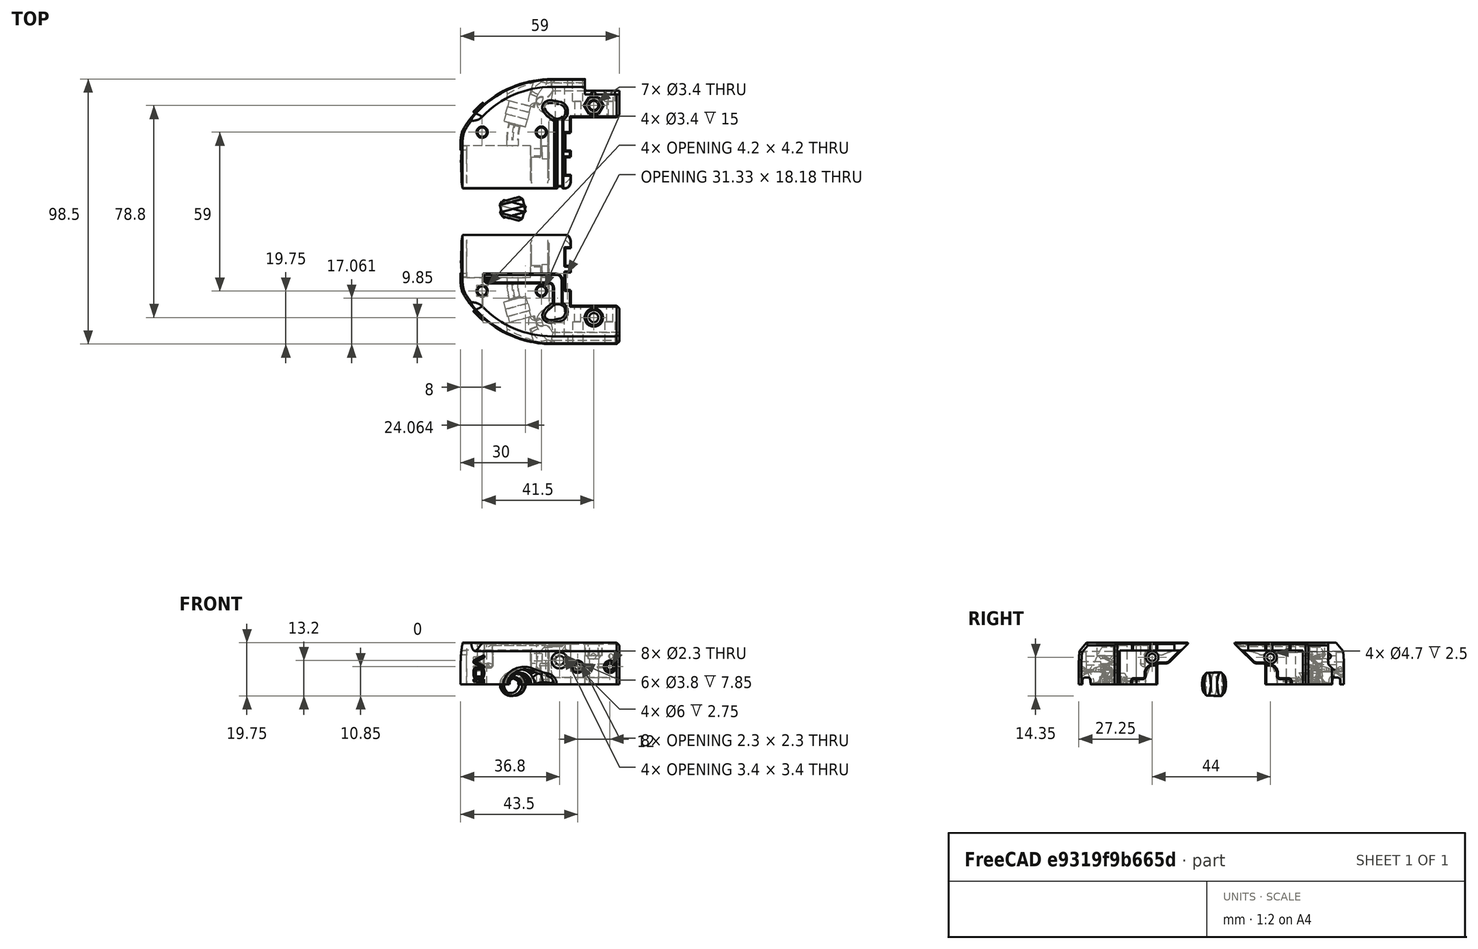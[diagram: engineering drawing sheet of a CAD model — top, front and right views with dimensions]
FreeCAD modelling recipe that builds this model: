
FCSTD DOCUMENT  (FreeCAD 0.18R16146 (Git))
Label: mosquito-toolhead-mod
License: All rights reserved
LicenseURL: http://en.wikipedia.org/wiki/All_rights_reserved
objects: Part::Cut×16, Part::Feature×12, Part::Cylinder×10, Part::Box×9, Part::MultiFuse×3, Part::Chamfer×2
note: 52 computed .brp shape members not serialized (recipe doc carries the construction recipe); baked Part::Feature solids carry a one-line shape summary decoded from their .brp

FEATURE [Part::Feature] Part__Feature154  label="Toolhead_Mosquito002"
  Placement = pos=(16.5,-1,0) rot=(0.707107,0,0.707107;3.14159rad)
  shape: bbox 59.02 x 41.29 x 24.92 mm, 349 faces (baked)
FEATURE [Part::Feature] Part__Feature155  label="Toolhead_Mosquito003"
  Placement = pos=(16.5,-1,0) rot=(0,1,0;1.5708rad)
  shape: bbox 59.02 x 41.29 x 24.92 mm, 379 faces (baked)
FEATURE [Part::Box] Box  label="Cube"
  AttacherType = Attacher::AttachEngine3D
  Height = 10
  Length = 12
  Placement = pos=(-4,-43,-10) rot=(0,0,1;0rad)
  Width = 10
FEATURE [Part::Cylinder] Cylinder  label="outer"
  Angle = 360
  AttacherType = Attacher::AttachEngine3D
  Height = 2.3
  Placement = pos=(0,0,0) rot=(0.983106,0.129428,0.129428;1.58783rad)
  Radius = 4.25
FEATURE [Part::Cylinder] Cylinder002  label="bore-vut"
  Angle = 360
  AttacherType = Attacher::AttachEngine3D
  Height = 2.6
  Placement = pos=(-0.67293,2.51141,-1e-15) rot=(0.983106,0.129428,0.129428;1.58783rad)
  Radius = 4.35
FEATURE [Part::Cylinder] Cylinder003  label="inner"
  Angle = 360
  AttacherType = Attacher::AttachEngine3D
  Height = 2.3
  Placement = pos=(0,0,0) rot=(0.983106,0.129428,0.129428;1.58783rad)
  Radius = 4.1
FEATURE [Part::Box] Box001  label="Cube001"
  AttacherType = Attacher::AttachEngine3D
  Height = 10
  Length = 12
  Placement = pos=(-4,-43,-10) rot=(0,0,1;0rad)
  Width = 10
FEATURE [Part::Box] Box002  label="Cube002"
  AttacherType = Attacher::AttachEngine3D
  Height = 10
  Length = 12
  Placement = pos=(-4,-43,-10) rot=(0,0,1;0rad)
  Width = 10
FEATURE [Part::Cylinder] Cylinder004  label="bore-vut001"
  Angle = 360
  AttacherType = Attacher::AttachEngine3D
  Height = 1.1
  Placement = pos=(-0.95763,3.57393,-1e-15) rot=(0.983106,0.129428,0.129428;1.58783rad)
  Radius = 4.35
FEATURE [Part::Chamfer] Chamfer
  Base = -> Cylinder004
  Edges = 1 edges r=1: [Edge3]
FEATURE [Part::Feature] Chamfer001
  Placement = pos=(2.04,-38.91,0) rot=(0,0,1;0rad)
  shape: bbox 8.429 x 3.055 x 8.7 mm, 4 faces (baked)
FEATURE [Part::Feature] Cylinder003001  label="inner001"
  Placement = pos=(2.04,-38.91,0) rot=(0,0,1;0rad)
  shape: bbox 8.516 x 4.344 x 8.2 mm, 3 faces (baked)
FEATURE [Part::Feature] Cylinder003002  label="outer001"
  Placement = pos=(2.04,-38.91,0) rot=(0,0,1;0rad)
  shape: bbox 8.806 x 4.422 x 8.5 mm, 3 faces (baked)
FEATURE [Part::Feature] Cylinder002001  label="bore-vut002"
  Placement = pos=(2.04,-38.91,0) rot=(0,0,1;0rad)
  shape: bbox 9.076 x 4.763 x 8.7 mm, 3 faces (baked)
FEATURE [Part::Box] Box003  label="Cube003"
  AttacherType = Attacher::AttachEngine3D
  Height = 10
  Length = 12
  Placement = pos=(-4,-43,-10) rot=(0,0,1;0rad)
  Width = 10
FEATURE [Part::Cut] Cut
  Base = -> Cylinder002001
  Tool = -> Box003
FEATURE [Part::Cut] Cut001
  Base = -> Cylinder003002
  Tool = -> Box
FEATURE [Part::Cut] Cut002
  Base = -> Cylinder003001
  Tool = -> Box001
FEATURE [Part::Cut] Cut003
  Base = -> Chamfer001
  Tool = -> Box002
FEATURE [Part::MultiFuse] Fusion
  Shapes = -> [Cut001,Part__Feature154]
FEATURE [Part::Cut] Cut004
  Base = -> Fusion
  Tool = -> Cut002
FEATURE [Part::Cut] Cut005
  Base = -> Cut004
  Tool = -> Cut
FEATURE [Part::Cut] Cut006
  Base = -> Cut005
  Tool = -> Cut003
FEATURE [Part::Cylinder] Cylinder003003  label="Cylinder"
  Angle = 360
  AttacherType = Attacher::AttachEngine3D
  Height = 2.3
  Placement = pos=(0,0,0) rot=(-0.983106,0.129428,-0.129428;1.58783rad)
  Radius = 4.25
FEATURE [Part::Cylinder] Cylinder003004  label="Cylinder001"
  Angle = 360
  AttacherType = Attacher::AttachEngine3D
  Height = 2.6
  Placement = pos=(-0.67293,-2.51141,2e-15) rot=(-0.983106,0.129428,-0.129428;1.58783rad)
  Radius = 4.25
FEATURE [Part::Cylinder] Cylinder003005  label="Cylinder002"
  Angle = 360
  AttacherType = Attacher::AttachEngine3D
  Height = 1.1
  Placement = pos=(-0.95763,-3.57393,3e-15) rot=(-0.983106,0.129428,-0.129428;1.58783rad)
  Radius = 4.25
FEATURE [Part::Chamfer] Chamfer002
  Base = -> Cylinder003005
  Edges = 1 edges r=1: [Edge3]
FEATURE [Part::Cylinder] Cylinder003006  label="Cylinder003"
  Angle = 360
  AttacherType = Attacher::AttachEngine3D
  Height = 2.3
  Placement = pos=(0,0,0) rot=(-0.983106,0.129428,-0.129428;1.58783rad)
  Radius = 4.1
FEATURE [Part::Feature] Cylinder003006001  label="Cylinder004"
  Placement = pos=(2.04,36.91,0) rot=(0,0,1;0rad)
  shape: bbox 8.516 x 4.344 x 8.2 mm, 3 faces (baked)
FEATURE [Part::Feature] Chamfer002001  label="Chamfer003"
  Placement = pos=(2.04,36.91,0) rot=(0,0,1;0rad)
  shape: bbox 8.236 x 3.004 x 8.5 mm, 4 faces (baked)
FEATURE [Part::Feature] Cylinder003004001  label="Cylinder005"
  Placement = pos=(2.04,36.91,0) rot=(0,0,1;0rad)
  shape: bbox 8.883 x 4.711 x 8.5 mm, 3 faces (baked)
FEATURE [Part::Feature] Cylinder003003001  label="Cylinder006"
  Placement = pos=(2.04,36.91,0) rot=(0,0,1;0rad)
  shape: bbox 8.806 x 4.422 x 8.5 mm, 3 faces (baked)
FEATURE [Part::Box] Box004  label="Cube004"
  AttacherType = Attacher::AttachEngine3D
  Height = 10
  Length = 14
  Placement = pos=(-5,29,-10) rot=(0,0,1;0rad)
  Width = 12
FEATURE [Part::Box] Box005  label="Cube005"
  AttacherType = Attacher::AttachEngine3D
  Height = 10
  Length = 14
  Placement = pos=(-5,29,-10) rot=(0,0,1;0rad)
  Width = 12
FEATURE [Part::Box] Box006  label="Cube006"
  AttacherType = Attacher::AttachEngine3D
  Height = 10
  Length = 14
  Placement = pos=(-5,29,-10) rot=(0,0,1;0rad)
  Width = 12
FEATURE [Part::Box] Box007  label="Cube007"
  AttacherType = Attacher::AttachEngine3D
  Height = 10
  Length = 14
  Placement = pos=(-5,29,-10) rot=(0,0,1;0rad)
  Width = 12
FEATURE [Part::Cut] Cut007
  Base = -> Cylinder003003001
  Tool = -> Box004
FEATURE [Part::Cut] Cut008
  Base = -> Cylinder003004001
  Tool = -> Box005
FEATURE [Part::Cut] Cut009
  Base = -> Chamfer002001
  Tool = -> Box006
FEATURE [Part::Cut] Cut010
  Base = -> Cylinder003006001
  Tool = -> Box007
FEATURE [Part::MultiFuse] Fusion001
  Shapes = -> [Cut007,Part__Feature155]
FEATURE [Part::Cut] Cut011
  Base = -> Fusion001
  Tool = -> Cut010
FEATURE [Part::Cut] Cut012
  Base = -> Cut011
  Tool = -> Cut008
FEATURE [Part::Cut] Cut013
  Base = -> Cut012
  Tool = -> Cut009
FEATURE [Part::Feature] Cut006001  label="Cut014"
  shape: bbox 59.02 x 41.29 x 24.92 mm, 350 faces (baked)
FEATURE [Part::Feature] Cut013001  label="Cut015"
  shape: bbox 59.02 x 41.29 x 24.92 mm, 381 faces (baked)
FEATURE [Part::Box] Box008  label="Cube008"
  AttacherType = Attacher::AttachEngine3D
  Height = 1.4
  Length = 3
  Placement = pos=(15.3,7.44,14) rot=(0,0,1;0rad)
  Width = 27
FEATURE [Part::Cut] Cut013002
  Base = -> Cut013001
  Tool = -> Box008
FEATURE [Part::Cylinder] Cylinder003006002  label="Cylinder007"
  Angle = 360
  AttacherType = Attacher::AttachEngine3D
  Height = 6
  Placement = pos=(30,38.4,9.4) rot=(0,0,1;0rad)
  Radius = 3.7
FEATURE [Part::Cylinder] Cylinder003006003  label="Cylinder008"
  Angle = 360
  AttacherType = Attacher::AttachEngine3D
  Height = 6
  Placement = pos=(30,38.4,9.4) rot=(0,0,1;0rad)
  Radius = 2
FEATURE [Part::MultiFuse] Fusion002
  Shapes = -> [Cut013002,Cylinder003006002]
FEATURE [Part::Cut] Cut013003
  Base = -> Fusion002
  Tool = -> Cylinder003006003
